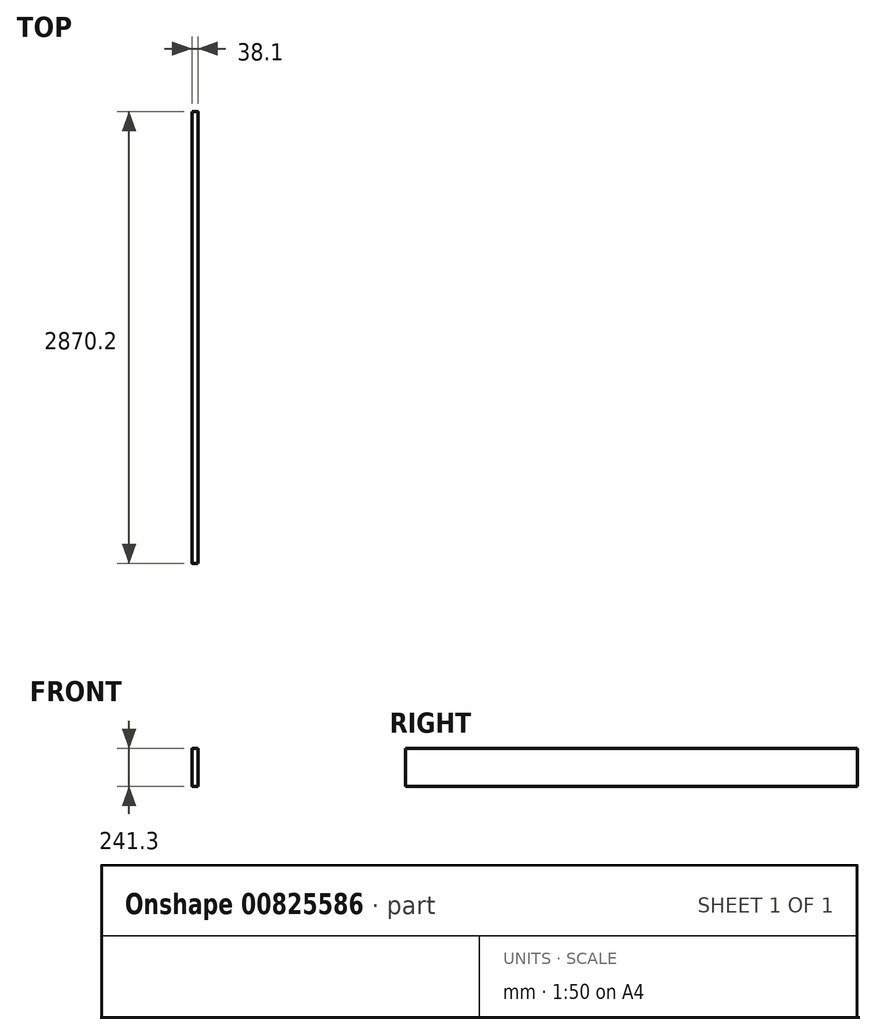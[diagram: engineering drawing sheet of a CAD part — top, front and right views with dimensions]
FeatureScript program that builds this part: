
annotation { "Feature Type Name" : "Feature", "Feature Type Description" : "" }
export const myFeature = defineFeature(function(context is Context, id is Id, definition is map)
    precondition{}
    {
        {
            var Q0;
            Q0=qCreatedBy(makeId("Front.planeOp"),FACE);
            var sketch = newSketch(context, id + "F0", { "sketchPlane" : qUnion([Q0])});
            skLineSegment(sketch, "E0.bottom", {"start": v(15.88, 120.65) * mm, "end": v(-15.87, 120.65) * mm});
            skLineSegment(sketch, "E0.top", {"start": v(15.88, -120.65) * mm, "end": v(-15.88, -120.65) * mm});
            skLineSegment(sketch, "E0.left", {"start": v(19.05, 117.47) * mm, "end": v(19.05, -117.48) * mm});
            skLineSegment(sketch, "E0.right", {"start": v(-19.05, 117.47) * mm, "end": v(-19.05, -117.48) * mm});
            skPoint(sketch, "E0.middle", {"position": v(0, 0) * mm});
            skPoint(sketch, "E1.visualSharp", {"position": v(-19.05, 120.65) * mm});
            skArc(sketch, "E1.filletArc", {"start": v(-15.87, 120.65) * mm, "mid": v(-18.12, 119.72) * mm, "end": v(-19.05, 117.48) * mm});
            skPoint(sketch, "E2.visualSharp", {"position": v(19.05, 120.65) * mm});
            skArc(sketch, "E2.filletArc", {"start": v(19.05, 117.47) * mm, "mid": v(18.12, 119.72) * mm, "end": v(15.88, 120.65) * mm});
            skPoint(sketch, "E3.visualSharp", {"position": v(19.05, -120.65) * mm});
            skArc(sketch, "E3.filletArc", {"start": v(15.88, -120.65) * mm, "mid": v(18.12, -119.72) * mm, "end": v(19.05, -117.48) * mm});
            skPoint(sketch, "E4.visualSharp", {"position": v(-19.05, -120.65) * mm});
            skArc(sketch, "E4.filletArc", {"start": v(-19.05, -117.48) * mm, "mid": v(-18.12, -119.72) * mm, "end": v(-15.88, -120.65) * mm});
            skSolve(sketch);
        }
        {
            var Q0;
            Q0=makeQuery(id+"F0.imprint","IMPRINT",FACE,{"disambiguationData":[TD([[makeQuery(id+"F0.imprint","IMPRINT",EDGE,{"derivedFrom":sQuery(id+"F0.wireOp",EDGE,"E0.bottom")}),1.0]])]});
            extrude(context, id + "F1", {"entities" : qUnion([Q0]), "endBound" : BoundingType.SYMMETRIC, "depth" : 2870.2 * mm, "offsetDistance" : 25.4 * mm});
        }
    });
